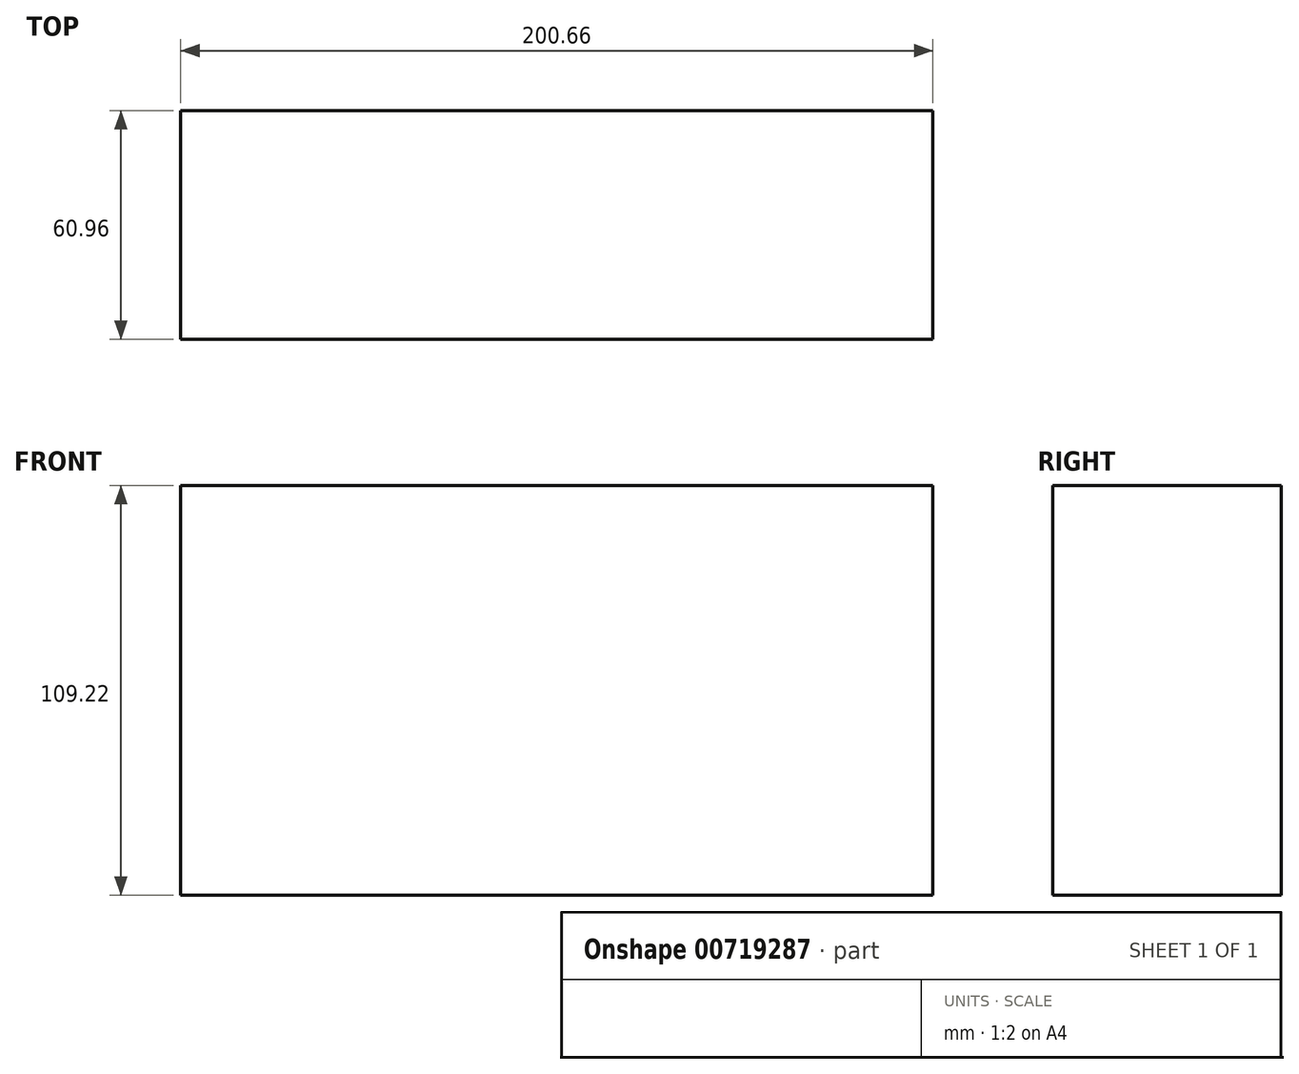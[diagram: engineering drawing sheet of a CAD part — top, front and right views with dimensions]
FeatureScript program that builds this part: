
annotation { "Feature Type Name" : "Feature", "Feature Type Description" : "" }
export const myFeature = defineFeature(function(context is Context, id is Id, definition is map)
    precondition{}
    {
        {
            var Q0;
            Q0=qCreatedBy(makeId("Top.planeOp"),FACE);
            var sketch = newSketch(context, id + "F0", { "sketchPlane" : qUnion([Q0])});
            skLineSegment(sketch, "E0.bottom", {"start": v(-100.33, 30.48) * mm, "end": v(100.33, 30.48) * mm});
            skLineSegment(sketch, "E0.top", {"start": v(-100.33, -30.48) * mm, "end": v(100.33, -30.48) * mm});
            skLineSegment(sketch, "E0.left", {"start": v(-100.33, 30.48) * mm, "end": v(-100.33, -30.48) * mm});
            skLineSegment(sketch, "E0.right", {"start": v(100.33, 30.48) * mm, "end": v(100.33, -30.48) * mm});
            skSolve(sketch);
        }
        {
            var Q0;
            Q0=makeQuery(id+"F0.imprint","IMPRINT",FACE,{"disambiguationData":[TD([[makeQuery(id+"F0.imprint","IMPRINT",EDGE,{"derivedFrom":sQuery(id+"F0.wireOp",EDGE,"E0.bottom")}),-1.0]])]});
            extrude(context, id + "F1", {"entities" : qUnion([Q0]), "depth" : 109.22 * mm, "offsetDistance" : 25.4 * mm});
        }
    });
